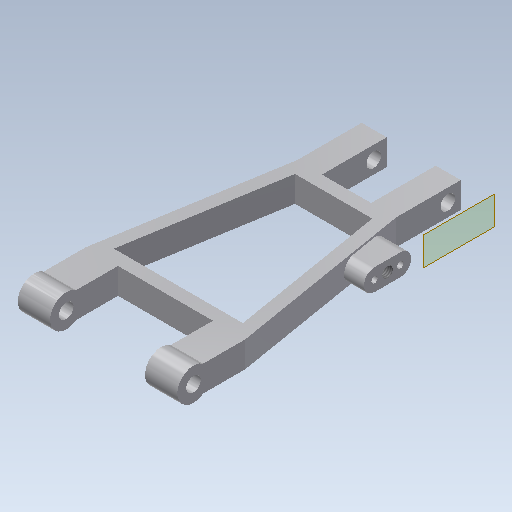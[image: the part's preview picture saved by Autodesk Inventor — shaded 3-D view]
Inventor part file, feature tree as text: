
AUTODESK INVENTOR PART (.ipt)
format: ipt  version: 2020 (Build 240168000, 168)  size: 210,432 bytes
history: native  units: mm
features: sketch x9, extrude x7, hole x3, plane x1
ambient origin geometry x8: Origin, YZ Plane, XZ Plane, XY Plane, X Axis, Y Axis, Z Axis, Center Point
bodies: Solid1 (feature_tree)
feature tree (20):
  extrude  "Extrusion1"  Depth=7.5mm
  extrude  "Extrusion2"  Depth=5.8mm
  extrude  "Extrusion3"  Depth=23.0mm
  extrude  "Extrusion4"  Depth=15.0mm
  extrude  "Extrusion5"  Depth=6.0mm TaperAngle=0.0deg
  extrude  "Extrusion6"  Depth=3.0mm
  hole  "Hole1"  [1 undecoded]
  plane  "Work Plane1"
  extrude  "Extrusion7"  Depth=6.0mm
  hole  "Hole2"  [1 undecoded]
  hole  "Hole3"  [1 undecoded]
  sketch  "Sketch1"  dims[d0=37.0mm d1=7.5mm]
  sketch  "Sketch2"  dims[d2=15.0mm d3=5.8mm]
  sketch  "Sketch3"  dims[d4=23.0mm d5=72.0mm]
  sketch  "Sketch4"  dims[d6=15.0mm d7=15.0mm]
  sketch  "Sketch5"  dims[d8=15.0mm d9=6.0mm d10=0.0mm]
  sketch  "Sketch6"  dims[d11=3.0mm d12=3.0mm]
  sketch  "Sketch7"  dims[d13=3.0mm d14=3.0mm]
  sketch  "Sketch8"  dims[d15=6.0mm d16=0.0mm d17=3.4mm]
  sketch  "Sketch9"  dims[d18=3.0mm d19=6.0mm d20=0.0mm d21=7.5mm d22=3.0mm d23=6.0mm d24=0.0mm d25=6.0mm d26=0.0mm d27=7.5mm d28=6.0mm d29=0.0mm d30=10.0mm d31=10.0mm d32=3.4mm d33=6.0mm d34=4.0mm d35=2.0mm d36=90.0deg d37=46.75mm d38=20.594885mm d39=-30.0mm d40=21.0mm d41=5.0mm d42=6.0mm d43=7.25mm d44=0.0mm d45=1.5mm d46=6.0mm d47=4.0mm d48=2.0mm d49=90.0deg d50=3.0mm d51=20.594885mm d52=2.459mm d53=6.0mm d54=4.0mm d55=2.0mm d56=90.0deg d57=10.8mm d58=20.594885mm]
note: 3 required parameter values undecoded (feature->parameter linkage not recoverable at this tier; creation-order binding heuristic only, values carry confidence <= 0.55)
